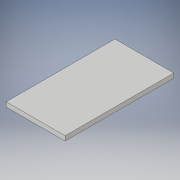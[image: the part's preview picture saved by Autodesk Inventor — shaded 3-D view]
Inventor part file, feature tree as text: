
AUTODESK INVENTOR PART (.ipt)
format: ipt  version: 2018 (Build 220112000, 112)  size: 89,600 bytes
history: native  units: in
note: dims shown in document units (in); Inventor stores cm internally (conversion verified against a paired STEP export)
features: extrude x1, sketch x1
ambient origin geometry x8: Origin, YZ Plane, XZ Plane, XY Plane, X Axis, Y Axis, Z Axis, Center Point
bodies: Solid1 (feature_tree)
feature tree (2):
  extrude  "Extrusion1"  Depth=24.0in
  sketch  "Sketch1"  dims[d0=13.0in d1=24.0in d2=1.0in d3=0.0in]
